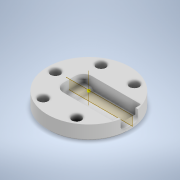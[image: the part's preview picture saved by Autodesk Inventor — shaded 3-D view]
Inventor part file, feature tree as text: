
AUTODESK INVENTOR PART (.ipt)
format: ipt  version: 2021 (Build 250183000, 183)  size: 749,568 bytes
history: native  units: in
note: dims shown in document units (in); Inventor stores cm internally (conversion verified against a paired STEP export)
features: sketch x8, extrude x6, fillet x4, chamfer x3, other x1, plane x1, pattern_circular x1, mirror x1
ambient origin geometry x8: Origin, YZ Plane, XZ Plane, XY Plane, X Axis, Y Axis, Z Axis, Center Point
bodies: Solid1 (feature_tree)
feature tree (25):
  extrude  "Extrusion1"  Depth=0.3701in TaperAngle=0.0deg
  chamfer  "Chamfer2"  Distance=0.2441in
  extrude  "Extrusion2"  Depth=0.1417in
  extrude  "Extrusion3"  Depth=0.2205in
  other  "Work Axis1"
  plane  "Work Plane1"
  extrude  "Extrusion5"  Depth=0.8268in
  extrude  "Extrusion4"  Depth=0.3539in
  fillet  "Fillet4"  Radius=0.1969in
  pattern_circular  "Circular Pattern2"  [2 undecoded]
  fillet  "Fillet7"  Radius=0.1417in
  extrude  "Initals"  TaperAngle=0.0deg  [1 undecoded]
  fillet  "Fillet9"  [1 undecoded]
  fillet  "Fillet10"  Radius=0.0394in
  mirror  "Mirror6"
  sketch  "Sketch18"  dims[d18=0.2047in d19=0.0in d23=0.8268in d24=0.3539in d31=0.1969in d32=0.063in d33=0.0in d44=0.1417in d47=0.0in d48=0.0in d49=0.0in d51=0.0in d54=0.0551in d55=0.0in d56=45.0deg d58=0.0394in d59=0.1181in d60=1.9685in d61=240.0deg d72=0.0315in d80=1.1811in d81=0.5906in d82=0.9728in d83=0.4864in d84=0.0394in d85=0.0in d86=0.547in d87=0.2735in d88=0.0787in d89=0.0in d90=0.0787in d98=0.1024in d99=0.0in d100=0.0in d101=0.2362in d102=0.0315in d103=0.0315in d104=0.2953in d105=0.1575in d106=0.1969in d107=0.063in d108=0.0787in d109=45.0deg d110=0.063in d111=0.0787in d112=45.0deg d91=0.0197in d92=0.0344in d93=0.0197in d94=0.0344in d120=0.0197in d121=0.0344in d122=0.0197in d123=0.0344in]
  chamfer  "Chamfer4"  Distance=0.1181in Angle=240.0deg
  chamfer  "Chamfer5"  Distance=0.0315in
  sketch  "Sketch1"  dims[d0=2.0472in d3=0.3701in d4=0.0in]
  sketch  "Sketch2"  dims[d5=1.4315in]
  sketch  "Sketch3"  dims[d6=0.7079in]
  sketch  "Sketch4"  dims[d7=0.3539in]
  sketch  "Sketch7"  dims[d8=0.4882in d9=0.2441in d10=0.0in]
  sketch  "Sketch12"  dims[d11=0.0in d14=0.1417in]
  sketch  "Sketch13"  dims[d15=0.0in d16=0.0in d17=0.2205in]
note: 4 required parameter values undecoded (feature->parameter linkage not recoverable at this tier; creation-order binding heuristic only, values carry confidence <= 0.55)
